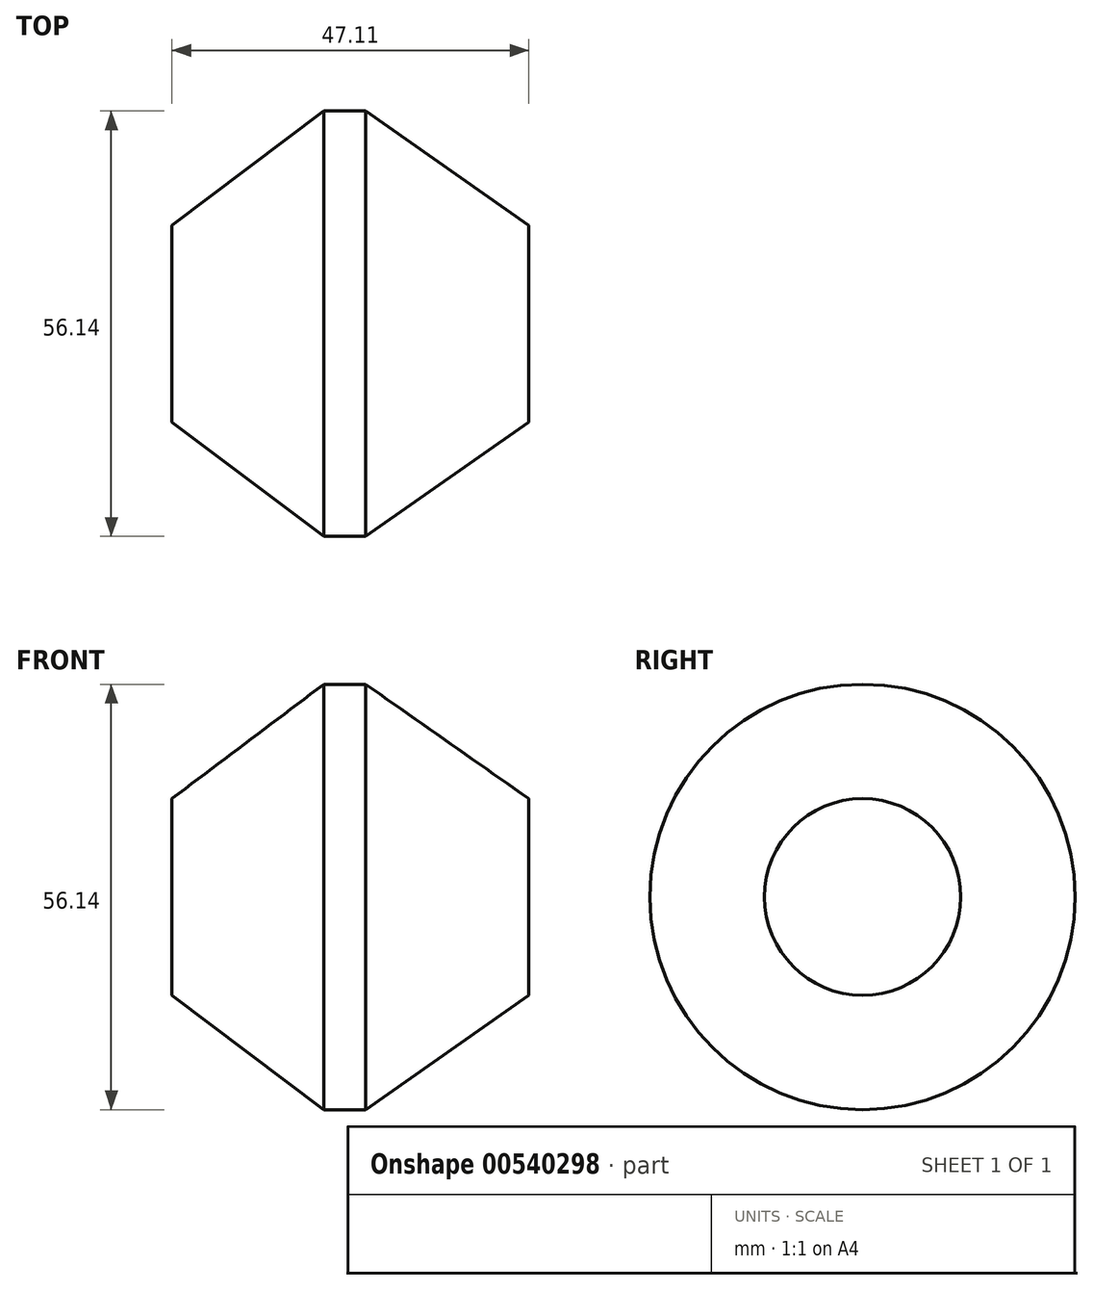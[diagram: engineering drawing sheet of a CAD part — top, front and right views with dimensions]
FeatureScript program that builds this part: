
annotation { "Feature Type Name" : "Feature", "Feature Type Description" : "" }
export const myFeature = defineFeature(function(context is Context, id is Id, definition is map)
    precondition{}
    {
        {
            var Q0;
            Q0=qCreatedBy(makeId("Front.planeOp"),FACE);
            var sketch = newSketch(context, id + "F0", { "sketchPlane" : qUnion([Q0])});
            skLineSegment(sketch, "E0", {"start": v(0, 0) * mm, "end": v(23.7, 0) * mm});
            skLineSegment(sketch, "E1", {"start": v(23.7, 0) * mm, "end": v(23.7, 12.97) * mm});
            skLineSegment(sketch, "E2", {"start": v(23.7, 12.97) * mm, "end": v(2.17, 28.07) * mm});
            skLineSegment(sketch, "E3", {"start": v(2.17, 28.07) * mm, "end": v(-3.37, 28.07) * mm});
            skLineSegment(sketch, "E4", {"start": v(-3.37, 28.07) * mm, "end": v(-23.4, 12.97) * mm});
            skLineSegment(sketch, "E5", {"start": v(-23.4, 12.97) * mm, "end": v(-23.4, 0) * mm});
            skLineSegment(sketch, "E6", {"start": v(-23.4, 0) * mm, "end": v(0, 0) * mm});
            skSolve(sketch);
        }
        {
            var Q0;
            Q0=makeQuery(id+"F0.imprint","IMPRINT",FACE,{"disambiguationData":[TD([[makeQuery(id+"F0.imprint","IMPRINT",EDGE,{"derivedFrom":sQuery(id+"F0.wireOp",EDGE,"E0")}),1.0]])]});
            var Q1;
            Q1=sQuery(id+"F0.wireOp",EDGE,"E0");
            revolve(context, id + "F1", {"entities" : qUnion([Q0]), "axis" : qUnion([Q1]), "revolveType" : RevolveType.FULL});
        }
    });
